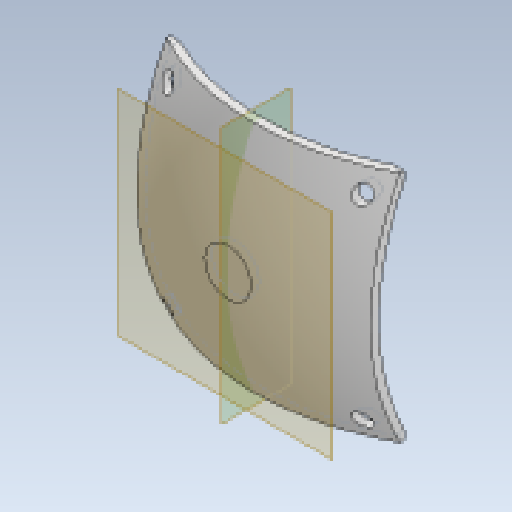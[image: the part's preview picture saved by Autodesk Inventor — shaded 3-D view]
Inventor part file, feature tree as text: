
AUTODESK INVENTOR PART (.ipt)
format: ipt  version: 2023 (Build 270158030, 158C)  size: 245,760 bytes
history: native  units: mm
features: other x5, sketch x3, reference x3, plane x2, extrude x2, revolve x1, projected_geometry x1
ambient origin geometry x8: Origin, YZ Plane, XZ Plane, XY Plane, X Axis, Y Axis, Z Axis, Center Point
bodies: Body1 (feature_tree)
feature tree (17):
  other  "sling"
  plane  "Work Plane1"
  extrude  "Extrusion1"  Depth=30.0mm
  plane  "Work Plane2"
  revolve  "Revolution1"  [1 undecoded]
  extrude  "Extrusion2"  Depth=1.0mm TaperAngle=0.0deg
  sketch  "Sketch1"  dims[d0=30.0mm d1=30.0mm]
  reference  "Reference1"
  reference  "Reference2"
  reference  "Reference3"
  sketch  "Sketch2"  dims[d2=15.0mm d3=12.5mm]
  projected_geometry  "Projected Loop1"
  sketch  "Sketch3"  dims[d4=12.5mm d5=8.0mm d6=0.0mm d7=360.0deg d9=15.0mm d19=15.0mm d20=11.0mm d21=11.0mm d22=4.0mm d24=2.0mm d25=2.5mm d26=2.5mm d27=2.5mm d28=2.5mm d29=0.0mm d30=0.0mm d31=1.0mm d32=0.4mm d33=1.0mm d34=3.0mm d35=35.0mm d36=36.0mm]
  other  "<userpath>\Documents\0004-inventor\3D-CAD-main\trebuchet\trebuchet-assembly.iam"
  other  "trebuchet-assembly.iam"
  other  "V1_baseplate:1"
  other  "bolder:1"
note: 1 required parameter value undecoded (feature->parameter linkage not recoverable at this tier; creation-order binding heuristic only, values carry confidence <= 0.55)
